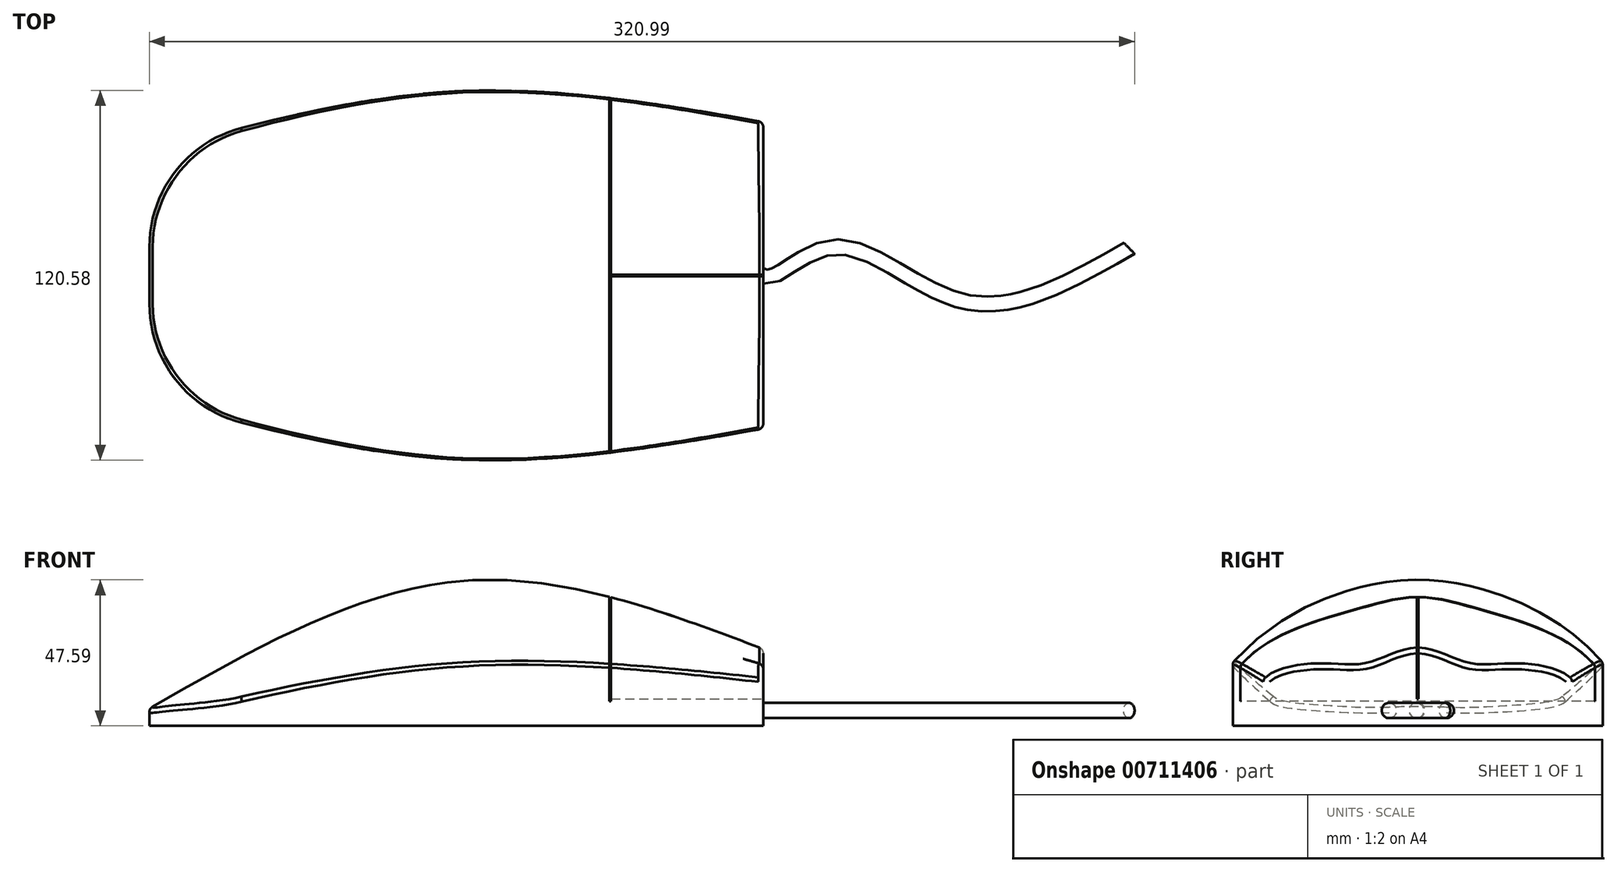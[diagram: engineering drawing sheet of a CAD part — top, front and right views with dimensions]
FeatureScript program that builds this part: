
annotation { "Feature Type Name" : "Feature", "Feature Type Description" : "" }
export const myFeature = defineFeature(function(context is Context, id is Id, definition is map)
    precondition{}
    {
        {
            var Q0;
            Q0=qCreatedBy(makeId("Right.planeOp"),FACE);
            var sketch = newSketch(context, id + "F0", { "sketchPlane" : qUnion([Q0])});
            skLineSegment(sketch, "E0", {"start": v(-40, 0) * mm, "end": v(40, 0) * mm});
            skLineSegment(sketch, "E1", {"start": v(40, 0) * mm, "end": v(40, 2) * mm});
            skLineSegment(sketch, "E2", {"start": v(-40, 2) * mm, "end": v(-40, 0) * mm});
            skFitSpline(sketch, "E3", {"points": [v(-40, 2) * mm, v(40, 2) * mm], "startDerivative": vector(82.27, 14.24) * mm, "endDerivative": vector(88.14, -15.14) * mm});
            skSolve(sketch);
        }
        {
            var Q0;
            Q0=qCreatedBy(makeId("Right.planeOp"),FACE);
            cPlane(context, id + "F1", {"entities" : qUnion([Q0]), "cplaneType" : CPlaneType.OFFSET, "offset" : 100 * mm, "width" : 150 * mm, "height" : 150 * mm});
        }
        {
            var Q0;
            Q0=qCreatedBy(id+"F1.planeOp",FACE);
            var sketch = newSketch(context, id + "F2", { "sketchPlane" : qUnion([Q0])});
            skLineSegment(sketch, "E4", {"start": v(-60, 20) * mm, "end": v(-60, 0) * mm});
            skLineSegment(sketch, "E5", {"start": v(-60, 0) * mm, "end": v(60, 0) * mm});
            skLineSegment(sketch, "E6", {"start": v(60, 0) * mm, "end": v(60, 20) * mm});
            skArc(sketch, "E7", {"start": v(60, 20) * mm, "mid": v(0, 47.08) * mm, "end": v(-60, 20) * mm});
            skSolve(sketch);
        }
        {
            var Q0;
            Q0=qCreatedBy(id+"F1.planeOp",FACE);
            cPlane(context, id + "F3", {"entities" : qUnion([Q0]), "cplaneType" : CPlaneType.OFFSET, "offset" : 100 * mm, "width" : 150 * mm, "height" : 150 * mm});
        }
        {
            var Q0;
            Q0=qCreatedBy(id+"F3.planeOp",FACE);
            var sketch = newSketch(context, id + "F4", { "sketchPlane" : qUnion([Q0])});
            skLineSegment(sketch, "E8", {"start": v(-50, 15) * mm, "end": v(-50, 0) * mm});
            skLineSegment(sketch, "E9", {"start": v(-50, 0) * mm, "end": v(50, 0) * mm});
            skLineSegment(sketch, "E10", {"start": v(50, 0) * mm, "end": v(50, 15) * mm});
            skFitSpline(sketch, "E11", {"points": [v(-50, 15) * mm, v(-30.75, 20) * mm, v(-15.97, 20.16) * mm, v(0, 25.06) * mm, v(15.97, 20.16) * mm, v(30.75, 20) * mm, v(50, 15) * mm], "startDerivative": vector(62.3, 66.82) * mm, "endDerivative": vector(62.3, -66.82) * mm});
            skSolve(sketch);
        }
        {
            var Q0;
            Q0=makeQuery(id+"F0.imprint","IMPRINT",FACE,{"disambiguationData":[TD([[makeQuery(id+"F0.imprint","IMPRINT",EDGE,{"derivedFrom":sQuery(id+"F0.wireOp",EDGE,"E0")}),1.0]])]});
            var Q1;
            Q1=makeQuery(id+"F2.imprint","IMPRINT",FACE,{"disambiguationData":[TD([[makeQuery(id+"F2.imprint","IMPRINT",EDGE,{"derivedFrom":sQuery(id+"F2.wireOp",EDGE,"E4")}),1.0]])]});
            var Q2;
            Q2=makeQuery(id+"F4.imprint","IMPRINT",FACE,{"disambiguationData":[TD([[makeQuery(id+"F4.imprint","IMPRINT",EDGE,{"derivedFrom":sQuery(id+"F4.wireOp",EDGE,"E8")}),1.0]])]});
            loft(context, id + "F5", {"sheetProfilesArray" : [{ "sheetProfileEntities" : qUnion([Q0]) }, { "sheetProfileEntities" : qUnion([Q1]) }, { "sheetProfileEntities" : qUnion([Q2]) }]});
        }
        {
            var Q0;
            Q0=makeQuery(id+"F5.opLoft","MID_CAP_EDGE",EDGE,{"disambiguationData":[OSD([sQuery(id+"F0.wireOp",EDGE,"E0"),sQuery(id+"F0.wireOp",EDGE,"E2"),sQuery(id+"F0.wireOp",EDGE,"E3")])],"capPos":0.0});
            var Q1;
            Q1=makeQuery(id+"F5.opLoft","MID_CAP_EDGE",EDGE,{"disambiguationData":[OSD([sQuery(id+"F0.wireOp",EDGE,"E0"),sQuery(id+"F0.wireOp",EDGE,"E1"),sQuery(id+"F0.wireOp",EDGE,"E3")])],"capPos":0.0});
            fillet(context, id + "F6", {"entities" : qUnion([Q0, Q1]), "radius" : 40 * mm, "allowEdgeOverflow" : false});
        }
        {
            var Q0;
            Q0=makeQuery(id+"F5.opLoft","CAP_FACE",FACE,{"disambiguationData":[OSD([makeQuery(id+"F4.imprint","IMPRINT",FACE,{"disambiguationData":[TD([[makeQuery(id+"F4.imprint","IMPRINT",EDGE,{"derivedFrom":sQuery(id+"F4.wireOp",EDGE,"E8")}),1.0]])]})])],"isStart":true});
            var sketch = newSketch(context, id + "F7", { "sketchPlane" : qUnion([Q0])});
            skLineSegment(sketch, "E12.bottom", {"start": v(0.25, 48.79) * mm, "end": v(-0.25, 48.79) * mm});
            skLineSegment(sketch, "E12.top", {"start": v(0.25, 8.79) * mm, "end": v(-0.25, 8.79) * mm});
            skLineSegment(sketch, "E12.left", {"start": v(0.25, 48.79) * mm, "end": v(0.25, 8.79) * mm});
            skLineSegment(sketch, "E12.right", {"start": v(-0.25, 48.79) * mm, "end": v(-0.25, 8.79) * mm});
            skPoint(sketch, "E12.middle", {"position": v(0, 28.79) * mm});
            skSolve(sketch);
        }
        {
            var Q0;
            Q0 = qSketchRegion(id + "F7", true);
            extrude(context, id + "F8", {"entities" : qUnion([Q0]), "operationType" : NewBodyOperationType.REMOVE, "oppositeDirection" : true, "depth" : 50 * mm, "offsetDistance" : 25 * mm});
        }
        {
            var Q0;
            Q0=qCreatedBy(makeId("Front.planeOp"),FACE);
            var sketch = newSketch(context, id + "F9", { "sketchPlane" : qUnion([Q0])});
            skLineSegment(sketch, "E13.bottom", {"start": v(150.42, 58.01) * mm, "end": v(149.92, 58.01) * mm});
            skLineSegment(sketch, "E13.top", {"start": v(150.42, 8.01) * mm, "end": v(149.92, 8.01) * mm});
            skLineSegment(sketch, "E13.left", {"start": v(150.42, 58.01) * mm, "end": v(150.42, 8.01) * mm});
            skLineSegment(sketch, "E13.right", {"start": v(149.92, 58.01) * mm, "end": v(149.92, 8.01) * mm});
            skPoint(sketch, "E13.middle", {"position": v(150.17, 33.01) * mm});
            skSolve(sketch);
        }
        {
            var Q0;
            Q0 = qSketchRegion(id + "F9", true);
            extrude(context, id + "F10", {"entities" : qUnion([Q0]), "operationType" : NewBodyOperationType.REMOVE, "endBound" : BoundingType.THROUGH_ALL, "oppositeDirection" : true, "depth" : 25 * mm, "offsetDistance" : 25 * mm});
        }
        {
            var Q0;
            Q0 = qSketchRegion(id + "F9", true);
            extrude(context, id + "F11", {"entities" : qUnion([Q0]), "operationType" : NewBodyOperationType.REMOVE, "endBound" : BoundingType.THROUGH_ALL, "depth" : 25 * mm, "offsetDistance" : 25 * mm});
        }
        {
            var Q0;
            {var subQ0=sQuery(id+"F2.wireOp",EDGE,"E7");var subQ1=sQuery(id+"F2.wireOp",EDGE,"E4");var subQ4=sQuery(id+"F9.wireOp",EDGE,"E13.right");Q0=makeQuery(id+"F11.boolean.opBoolean","SPLIT",EDGE,{"disambiguationData":[TD([makeQuery(id+"F10.boolean.opBoolean","COPY",FACE,{"derivedFrom":makeQuery(id+"F10.opExtrude","SWEPT_FACE",FACE,{"disambiguationData":[OSD([subQ4])]})})])],"derivedFrom":makeQuery(id+"F5.opLoft","SWEPT_EDGE",EDGE,{"disambiguationData":[OSD([subQ1,subQ0,sQuery(id+"F4.wireOp",EDGE,"E8"),sQuery(id+"F4.wireOp",EDGE,"E11")])]})});}
            var Q1;
            {var subQ0=sQuery(id+"F9.wireOp",EDGE,"E13.left");var subQ1=sQuery(id+"F4.wireOp",EDGE,"E8");var subQ2=sQuery(id+"F4.wireOp",EDGE,"E11");var subQ3=sQuery(id+"F2.wireOp",EDGE,"E7");var subQ4=sQuery(id+"F2.wireOp",EDGE,"E4");Q1=makeQuery(id+"F11.boolean.opBoolean","SPLIT",EDGE,{"disambiguationData":[TD([makeQuery(id+"F10.boolean.opBoolean","COPY",FACE,{"derivedFrom":makeQuery(id+"F10.opExtrude","SWEPT_FACE",FACE,{"disambiguationData":[OSD([subQ0])]})})])],"derivedFrom":makeQuery(id+"F5.opLoft","SWEPT_EDGE",EDGE,{"disambiguationData":[OSD([subQ4,subQ3,subQ1,subQ2])]})});}
            var Q2;
            {var subQ4=sQuery(id+"F4.wireOp",EDGE,"E8");var subQ5=sQuery(id+"F4.wireOp",EDGE,"E10");var subQ6=sQuery(id+"F4.wireOp",EDGE,"E11");Q2=makeQuery(id+"F8.boolean.opBoolean","SPLIT",EDGE,{"disambiguationData":[TD([makeQuery(id+"F8.opExtrude","SWEPT_FACE",FACE,{"disambiguationData":[OSD([sQuery(id+"F7.wireOp",EDGE,"E12.right")])]})])],"derivedFrom":makeQuery(id+"F5.opLoft","MID_CAP_EDGE",EDGE,{"disambiguationData":[OSD([subQ4,subQ5,subQ6])],"capPos":2.0})});}
            var Q3;
            {var subQ4=sQuery(id+"F4.wireOp",EDGE,"E8");var subQ5=sQuery(id+"F4.wireOp",EDGE,"E10");var subQ6=sQuery(id+"F4.wireOp",EDGE,"E11");Q3=makeQuery(id+"F8.boolean.opBoolean","SPLIT",EDGE,{"disambiguationData":[TD([makeQuery(id+"F8.opExtrude","SWEPT_FACE",FACE,{"disambiguationData":[OSD([sQuery(id+"F7.wireOp",EDGE,"E12.left")])]})])],"derivedFrom":makeQuery(id+"F5.opLoft","MID_CAP_EDGE",EDGE,{"disambiguationData":[OSD([subQ4,subQ5,subQ6])],"capPos":2.0})});}
            var Q4;
            {var subQ0=sQuery(id+"F2.wireOp",EDGE,"E7");var subQ1=sQuery(id+"F2.wireOp",EDGE,"E6");var subQ4=sQuery(id+"F4.wireOp",EDGE,"E10");var subQ5=sQuery(id+"F4.wireOp",EDGE,"E11");Q4=makeQuery(id+"F10.boolean.opBoolean","SPLIT",EDGE,{"disambiguationData":[TD([makeQuery(id+"F10.opExtrude","SWEPT_FACE",FACE,{"disambiguationData":[OSD([sQuery(id+"F9.wireOp",EDGE,"E13.left")])]})])],"derivedFrom":makeQuery(id+"F5.opLoft","SWEPT_EDGE",EDGE,{"disambiguationData":[OSD([subQ1,subQ0,subQ4,subQ5])]})});}
            var Q5;
            Q5=makeQuery(id+"F5.opLoft","MID_CAP_EDGE",EDGE,{"disambiguationData":[OSD([sQuery(id+"F4.wireOp",EDGE,"E8"),sQuery(id+"F4.wireOp",EDGE,"E9"),sQuery(id+"F4.wireOp",EDGE,"E11")])],"capPos":2.0});
            var Q6;
            Q6=makeQuery(id+"F5.opLoft","MID_CAP_EDGE",EDGE,{"disambiguationData":[OSD([sQuery(id+"F4.wireOp",EDGE,"E9"),sQuery(id+"F4.wireOp",EDGE,"E10"),sQuery(id+"F4.wireOp",EDGE,"E11")])],"capPos":2.0});
            fillet(context, id + "F12", {"entities" : qUnion([Q0, Q1, Q2, Q3, Q4, Q5, Q6]), "radius" : 2 * mm, "tangentPropagation" : true, "allowEdgeOverflow" : false});
        }
        {
            var Q0;
            Q0=qCreatedBy(makeId("Top.planeOp"),FACE);
            cPlane(context, id + "F13", {"entities" : qUnion([Q0]), "cplaneType" : CPlaneType.OFFSET, "offset" : 5 * mm, "width" : 150 * mm, "height" : 150 * mm});
        }
        {
            var Q0;
            Q0=qCreatedBy(id+"F13.planeOp",FACE);
            var sketch = newSketch(context, id + "F14", { "sketchPlane" : qUnion([Q0])});
            skFitSpline(sketch, "E14", {"points": [v(199.36, 0) * mm, v(203.48, 0) * mm, v(224.3, 9.32) * mm, v(265.7, -8.6) * mm, v(319.22, 8.84) * mm], "startDerivative": vector(35.93, -11.04) * mm, "endDerivative": vector(153.9, 88.79) * mm});
            skSolve(sketch);
        }
        {
            var Q0;
            Q0=qCreatedBy(id+"F3.planeOp",FACE);
            var sketch = newSketch(context, id + "F15", { "sketchPlane" : qUnion([Q0])});
            skCircle(sketch, "E15", {"center": v(-0.19, 5) * mm, "radius": 2.5 * mm});
            skSolve(sketch);
        }
        {
            var Q0;
            Q0=makeQuery(id+"F15.imprint","IMPRINT",FACE,{"disambiguationData":[TD([[makeQuery(id+"F15.imprint","IMPRINT",EDGE,{"derivedFrom":sQuery(id+"F15.wireOp",EDGE,"E15")}),1.0]])]});
            var Q1;
            Q1=sQuery(id+"F14.wireOp",EDGE,"E14");
            sweep(context, id + "F16", {"operationType" : NewBodyOperationType.ADD, "profiles" : qUnion([Q0]), "path" : qUnion([Q1])});
        }
    });
